# Revit family: NLRS_74_PF_UN_bad_S8VR1010000_SPHINX_BCB
name_source: partatom
category: Plumbing Fixtures
revit_build: Autodesk Revit 2016 (Build: 20150220_1215(x64)
units: mm (PartAtom-declared; Revit-internal decimal feet)

## family parameters
Always vertical = Yes
Cut with Voids When Loaded = No
OmniClass Number = 23.45.00.00
OmniClass Title = Sanitary, Laundry, and Cleaning Equipment
Part Type = Normal
Room Calculation Point = No
Round Connector Dimension = Use Radius
Shared = No
Work Plane-Based = No

## types (2) — shared parameters
Keynote = kinderbad 91cm
Manufacturer = Sphinx
Model = 300 kids 91
NLRS_S_gewicht = 0.00 kg
Waste Connection = Yes
radius = 25 mm  [stored 0.082021 ft]
zero-valued in all types: WFU

## per-type parameters (varying)
| type | Assembly Code | Description | IfcElement | IfcExportAs | IfcExportType | IfcTypeProduct | NLRS_C_URL_BCB | NLRS_C_breedte | NLRS_C_code_EAN | NLRS_C_code_artikel | NLRS_C_content_datum_gewijzigd | NLRS_C_content_datum_uitgifte | NLRS_C_content_provider | NLRS_C_content_versie | NLRS_C_diameter_uit | NLRS_C_hoogte | NLRS_C_lengte | NLRS_C_materiaal | NLRS_C_revit_versie | URL |
| 300 kids 91 |  | bad | IfcFlowTerminal | IfcSanitaryTerminalTypeEnum | BATH | IfcSanitaryTerminalType | http://bcb-online.nl | 515 mm  [stored 1.68963 ft] | 8711754390607 | S8VR1009000 | APR-2018 | APR-2018 | BouwConnect | 2.0 | 50 mm  [stored 0.164042 ft] | 257 mm  [stored 0.843176 ft] | 910 mm  [stored 2.98556 ft] | NLRS_n6_acryl_wit_Sphinx | 2016 | http://www.sphinx.nl |
| SPHINX_-_Sphinx_300_Varicor_-_Kinderbadje_91_conn | 4(74.11) | Sphinx - 300 kids 91 |  |  |  |  |  | 0 mm  [stored 0 ft] |  |  |  |  |  |  | 0 mm  [stored 0 ft] | 0 mm  [stored 0 ft] | 0 mm  [stored 0 ft] | <By Category> |  |  |

note: [stored X ft] marks values corroborated as IEEE doubles in the binary element streams (Revit-internal decimal feet)

## geometry (parser evidence)
native form markers: Blend x4, Sweep x3
no freeform markers — native parametric forms only
